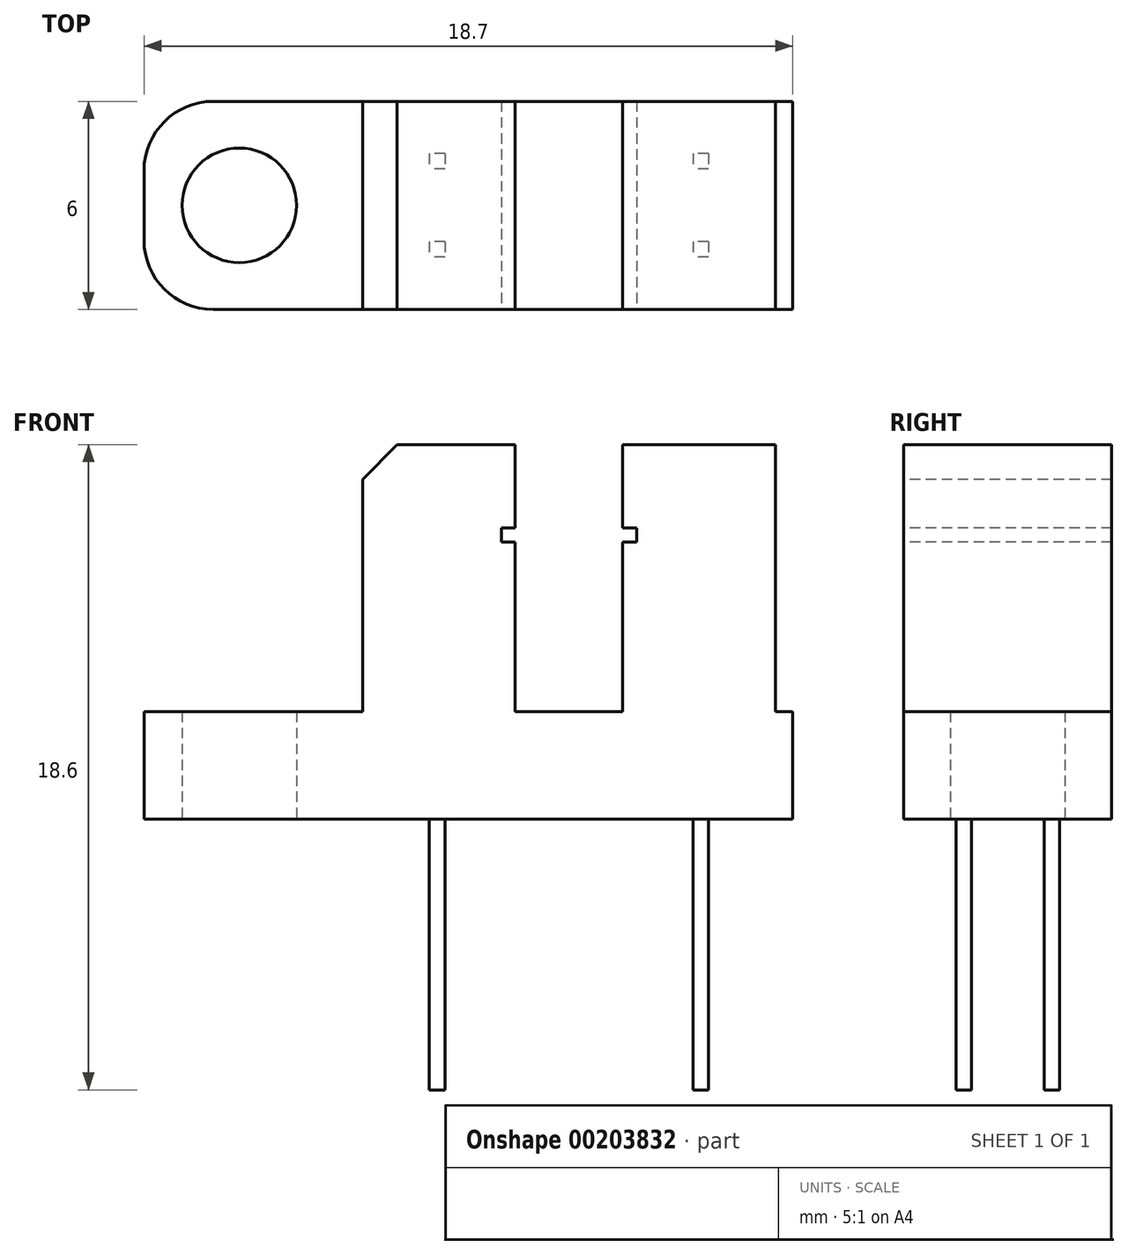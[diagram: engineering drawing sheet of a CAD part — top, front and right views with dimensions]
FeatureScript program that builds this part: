
annotation { "Feature Type Name" : "Feature", "Feature Type Description" : "" }
export const myFeature = defineFeature(function(context is Context, id is Id, definition is map)
    precondition{}
    {
        {
            var Q0;
            Q0=qCreatedBy(makeId("Front.planeOp"),FACE);
            var sketch = newSketch(context, id + "F0", { "sketchPlane" : qUnion([Q0])});
            skLineSegment(sketch, "E0.bottom", {"start": v(12.25, 0) * mm, "end": v(-12.25, 0) * mm});
            skLineSegment(sketch, "E0.top", {"start": v(12.25, 3.1) * mm, "end": v(5.95, 3.1) * mm});
            skLineSegment(sketch, "E0.left", {"start": v(12.25, 0) * mm, "end": v(12.25, 3.1) * mm});
            skLineSegment(sketch, "E0.right", {"start": v(-12.25, 0) * mm, "end": v(-12.25, 3.1) * mm});
            skPoint(sketch, "E0.middle", {"position": v(0, 1.55) * mm});
            skLineSegment(sketch, "E1.bottom", {"start": v(1.55, 3.1) * mm, "end": v(-1.55, 3.1) * mm});
            skLineSegment(sketch, "E1.top", {"start": v(5.95, 10.8) * mm, "end": v(1.55, 10.8) * mm});
            skLineSegment(sketch, "E1.left", {"start": v(5.95, 3.1) * mm, "end": v(5.95, 10.8) * mm});
            skLineSegment(sketch, "E1.right", {"start": v(-5.95, 3.1) * mm, "end": v(-5.95, 9.8) * mm});
            skPoint(sketch, "E1.middle", {"position": v(0, 6.95) * mm});
            skLineSegment(sketch, "E2.left", {"start": v(1.55, 3.1) * mm, "end": v(1.55, 8) * mm});
            skLineSegment(sketch, "E2.right", {"start": v(-1.55, 3.1) * mm, "end": v(-1.55, 8) * mm});
            skLineSegment(sketch, "E3.trimOffspring", {"start": v(-1.55, 10.8) * mm, "end": v(-4.95, 10.8) * mm});
            skLineSegment(sketch, "E4", {"start": v(-4.95, 10.8) * mm, "end": v(-5.95, 9.8) * mm});
            skPoint(sketch, "E5.orphan", {"position": v(-5.95, 10.8) * mm});
            skLineSegment(sketch, "E6.trimOffspring", {"start": v(-5.95, 3.1) * mm, "end": v(-12.25, 3.1) * mm});
            skLineSegment(sketch, "E7.bottom", {"start": v(-1.55, 8.4) * mm, "end": v(-1.95, 8.4) * mm});
            skLineSegment(sketch, "E7.top", {"start": v(-1.55, 8) * mm, "end": v(-1.95, 8) * mm});
            skLineSegment(sketch, "E7.right", {"start": v(-1.95, 8.4) * mm, "end": v(-1.95, 8) * mm});
            skLineSegment(sketch, "E8.trimOffspring", {"start": v(-1.55, 8.4) * mm, "end": v(-1.55, 10.8) * mm});
            skLineSegment(sketch, "E9.bottom", {"start": v(1.55, 8.4) * mm, "end": v(1.95, 8.4) * mm});
            skLineSegment(sketch, "E9.top", {"start": v(1.55, 8) * mm, "end": v(1.95, 8) * mm});
            skLineSegment(sketch, "E9.right", {"start": v(1.95, 8.4) * mm, "end": v(1.95, 8) * mm});
            skLineSegment(sketch, "E10.trimOffspring", {"start": v(1.55, 8.4) * mm, "end": v(1.55, 10.8) * mm});
            skSolve(sketch);
        }
        {
            var Q0;
            Q0 = qSketchRegion(id + "F0", true);
            extrude(context, id + "F1", {"entities" : qUnion([Q0]), "oppositeDirection" : true, "depth" : 6 * mm});
        }
        {
            var Q0;
            Q0=makeQuery(id+"F1.opExtrude","CAP_EDGE",EDGE,{"disambiguationData":[OSD([sQuery(id+"F0.wireOp",EDGE,"E0.right")])],"isStart":true});
            var Q1;
            Q1=makeQuery(id+"F1.opExtrude","CAP_EDGE",EDGE,{"disambiguationData":[OSD([sQuery(id+"F0.wireOp",EDGE,"E0.left")])],"isStart":true});
            var Q2;
            Q2=makeQuery(id+"F1.opExtrude","CAP_EDGE",EDGE,{"disambiguationData":[OSD([sQuery(id+"F0.wireOp",EDGE,"E0.left")])],"isStart":false});
            var Q3;
            Q3=makeQuery(id+"F1.opExtrude","CAP_EDGE",EDGE,{"disambiguationData":[OSD([sQuery(id+"F0.wireOp",EDGE,"E0.right")])],"isStart":false});
            fillet(context, id + "F2", {"entities" : qUnion([Q0, Q1, Q2, Q3]), "radius" : 2 * mm, "tangentPropagation" : true, "allowEdgeOverflow" : false});
        }
        {
            var Q0;
            Q0=makeQuery(id+"F1.opExtrude","SWEPT_FACE",FACE,{"disambiguationData":[OSD([sQuery(id+"F0.wireOp",EDGE,"E0.bottom")])]});
            var sketch = newSketch(context, id + "F3", { "sketchPlane" : qUnion([Q0])});
            skCircle(sketch, "E11", {"center": v(-9.5, -3) * mm, "radius": 1.65 * mm});
            skCircle(sketch, "E12", {"center": v(9.5, -3) * mm, "radius": 1.65 * mm});
            skLineSegment(sketch, "E13.bottom", {"start": v(-3.57, -1.95) * mm, "end": v(-4.02, -1.95) * mm});
            skLineSegment(sketch, "E13.top", {"start": v(-3.57, -1.5) * mm, "end": v(-4.02, -1.5) * mm});
            skLineSegment(sketch, "E13.left", {"start": v(-3.57, -1.95) * mm, "end": v(-3.57, -1.5) * mm});
            skLineSegment(sketch, "E13.right", {"start": v(-4.02, -1.95) * mm, "end": v(-4.02, -1.5) * mm});
            skPoint(sketch, "E13.middle", {"position": v(-3.8, -1.73) * mm});
            skLineSegment(sketch, "E14.bottom", {"start": v(-3.57, -4.5) * mm, "end": v(-4.02, -4.5) * mm});
            skLineSegment(sketch, "E14.top", {"start": v(-3.57, -4.04) * mm, "end": v(-4.02, -4.04) * mm});
            skLineSegment(sketch, "E14.left", {"start": v(-3.57, -4.5) * mm, "end": v(-3.57, -4.04) * mm});
            skLineSegment(sketch, "E14.right", {"start": v(-4.02, -4.5) * mm, "end": v(-4.02, -4.04) * mm});
            skPoint(sketch, "E14.middle", {"position": v(-3.8, -4.27) * mm});
            skLineSegment(sketch, "E15.bottom", {"start": v(4.03, -4.5) * mm, "end": v(3.58, -4.5) * mm});
            skLineSegment(sketch, "E15.top", {"start": v(4.03, -4.04) * mm, "end": v(3.58, -4.04) * mm});
            skLineSegment(sketch, "E15.left", {"start": v(4.03, -4.5) * mm, "end": v(4.03, -4.04) * mm});
            skLineSegment(sketch, "E15.right", {"start": v(3.58, -4.5) * mm, "end": v(3.58, -4.04) * mm});
            skPoint(sketch, "E15.middle", {"position": v(3.8, -4.27) * mm});
            skLineSegment(sketch, "E16.bottom", {"start": v(4.03, -1.95) * mm, "end": v(3.58, -1.95) * mm});
            skLineSegment(sketch, "E16.top", {"start": v(4.03, -1.5) * mm, "end": v(3.58, -1.5) * mm});
            skLineSegment(sketch, "E16.left", {"start": v(4.03, -1.95) * mm, "end": v(4.03, -1.5) * mm});
            skLineSegment(sketch, "E16.right", {"start": v(3.58, -1.95) * mm, "end": v(3.58, -1.5) * mm});
            skPoint(sketch, "E16.middle", {"position": v(3.8, -1.73) * mm});
            skPoint(sketch, "E17", {"position": v(0, -3) * mm});
            skSolve(sketch);
        }
        {
            var Q0;
            Q0=makeQuery(id+"F3.imprint","IMPRINT",FACE,{"disambiguationData":[TD([[makeQuery(id+"F3.imprint","IMPRINT",EDGE,{"derivedFrom":sQuery(id+"F3.wireOp",EDGE,"E11")}),1.0]])]});
            var Q1;
            Q1=makeQuery(id+"F3.imprint","IMPRINT",FACE,{"disambiguationData":[TD([[makeQuery(id+"F3.imprint","IMPRINT",EDGE,{"derivedFrom":sQuery(id+"F3.wireOp",EDGE,"E12")}),1.0]])]});
            extrude(context, id + "F4", {"entities" : qUnion([Q0, Q1]), "operationType" : NewBodyOperationType.REMOVE, "endBound" : BoundingType.UP_TO_NEXT, "oppositeDirection" : true, "depth" : 25 * mm});
        }
        {
            var Q0;
            Q0=makeQuery(id+"F3.imprint","IMPRINT",FACE,{"disambiguationData":[TD([[makeQuery(id+"F3.imprint","IMPRINT",EDGE,{"derivedFrom":sQuery(id+"F3.wireOp",EDGE,"E13.bottom")}),-1.0]])]});
            var Q1;
            Q1=makeQuery(id+"F3.imprint","IMPRINT",FACE,{"disambiguationData":[TD([[makeQuery(id+"F3.imprint","IMPRINT",EDGE,{"derivedFrom":sQuery(id+"F3.wireOp",EDGE,"E14.bottom")}),-1.0]])]});
            var Q2;
            Q2=makeQuery(id+"F3.imprint","IMPRINT",FACE,{"disambiguationData":[TD([[makeQuery(id+"F3.imprint","IMPRINT",EDGE,{"derivedFrom":sQuery(id+"F3.wireOp",EDGE,"E15.bottom")}),-1.0]])]});
            var Q3;
            Q3=makeQuery(id+"F3.imprint","IMPRINT",FACE,{"disambiguationData":[TD([[makeQuery(id+"F3.imprint","IMPRINT",EDGE,{"derivedFrom":sQuery(id+"F3.wireOp",EDGE,"E16.bottom")}),-1.0]])]});
            extrude(context, id + "F5", {"entities" : qUnion([Q0, Q1, Q2, Q3]), "operationType" : NewBodyOperationType.ADD, "depth" : 7.8 * mm});
        }
        {
            var Q0;
            Q0=makeQuery(id+"F1.opExtrude","SWEPT_FACE",FACE,{"disambiguationData":[OSD([sQuery(id+"F0.wireOp",EDGE,"E0.top")])]});
            var sketch = newSketch(context, id + "F6", { "sketchPlane" : qUnion([Q0])});
            skLineSegment(sketch, "E18.bottom", {"start": v(6.45, 6) * mm, "end": v(12.25, 6) * mm});
            skLineSegment(sketch, "E18.top", {"start": v(6.45, 0) * mm, "end": v(12.25, 0) * mm});
            skLineSegment(sketch, "E18.left", {"start": v(6.45, 6) * mm, "end": v(6.45, 0) * mm});
            skLineSegment(sketch, "E18.right", {"start": v(12.25, 6) * mm, "end": v(12.25, 0) * mm});
            skSolve(sketch);
        }
        {
            var Q0;
            {var subQ7=sQuery(id+"F6.wireOp",EDGE,"E18.left");Q0=makeQuery(id+"F6.imprint","IMPRINT",FACE,{"disambiguationData":[TD([[makeQuery(id+"F6.imprint","IMPRINT",EDGE,{"derivedFrom":subQ7}),1.0]])]});}
            extrude(context, id + "F7", {"entities" : qUnion([Q0]), "operationType" : NewBodyOperationType.REMOVE, "endBound" : BoundingType.UP_TO_NEXT, "oppositeDirection" : true, "depth" : 25 * mm});
        }
    });
